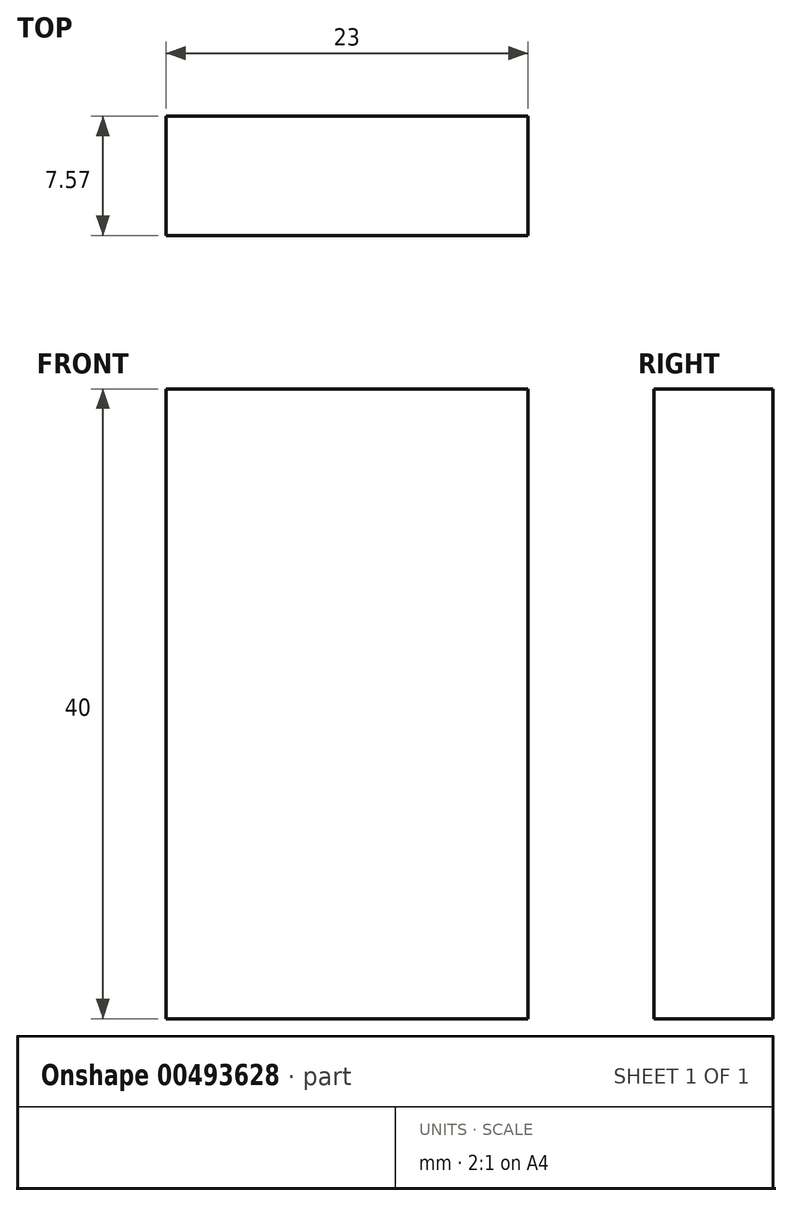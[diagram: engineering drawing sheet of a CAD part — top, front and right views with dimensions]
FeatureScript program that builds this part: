
annotation { "Feature Type Name" : "Feature", "Feature Type Description" : "" }
export const myFeature = defineFeature(function(context is Context, id is Id, definition is map)
    precondition{}
    {
        {
            var Q0;
            Q0=qCreatedBy(makeId("Front.planeOp"),FACE);
            var sketch = newSketch(context, id + "F0", { "sketchPlane" : qUnion([Q0])});
            skLineSegment(sketch, "E0.bottom", {"start": v(12.1, 20) * mm, "end": v(-10.9, 20) * mm});
            skLineSegment(sketch, "E0.top", {"start": v(12.1, -20) * mm, "end": v(-10.9, -20) * mm});
            skLineSegment(sketch, "E0.left", {"start": v(12.1, 20) * mm, "end": v(12.1, -20) * mm});
            skLineSegment(sketch, "E0.right", {"start": v(-10.9, 20) * mm, "end": v(-10.9, -20) * mm});
            skPoint(sketch, "E0.middle", {"position": v(0.6, 0) * mm});
            skSolve(sketch);
        }
        {
            var Q0;
            Q0=makeQuery(id+"F0.imprint","IMPRINT",FACE,{"disambiguationData":[TD([[makeQuery(id+"F0.imprint","IMPRINT",EDGE,{"derivedFrom":sQuery(id+"F0.wireOp",EDGE,"E0.bottom")}),1.0]])]});
            extrude(context, id + "F1", {"entities" : qUnion([Q0]), "depth" : 7.57 * mm});
        }
    });
